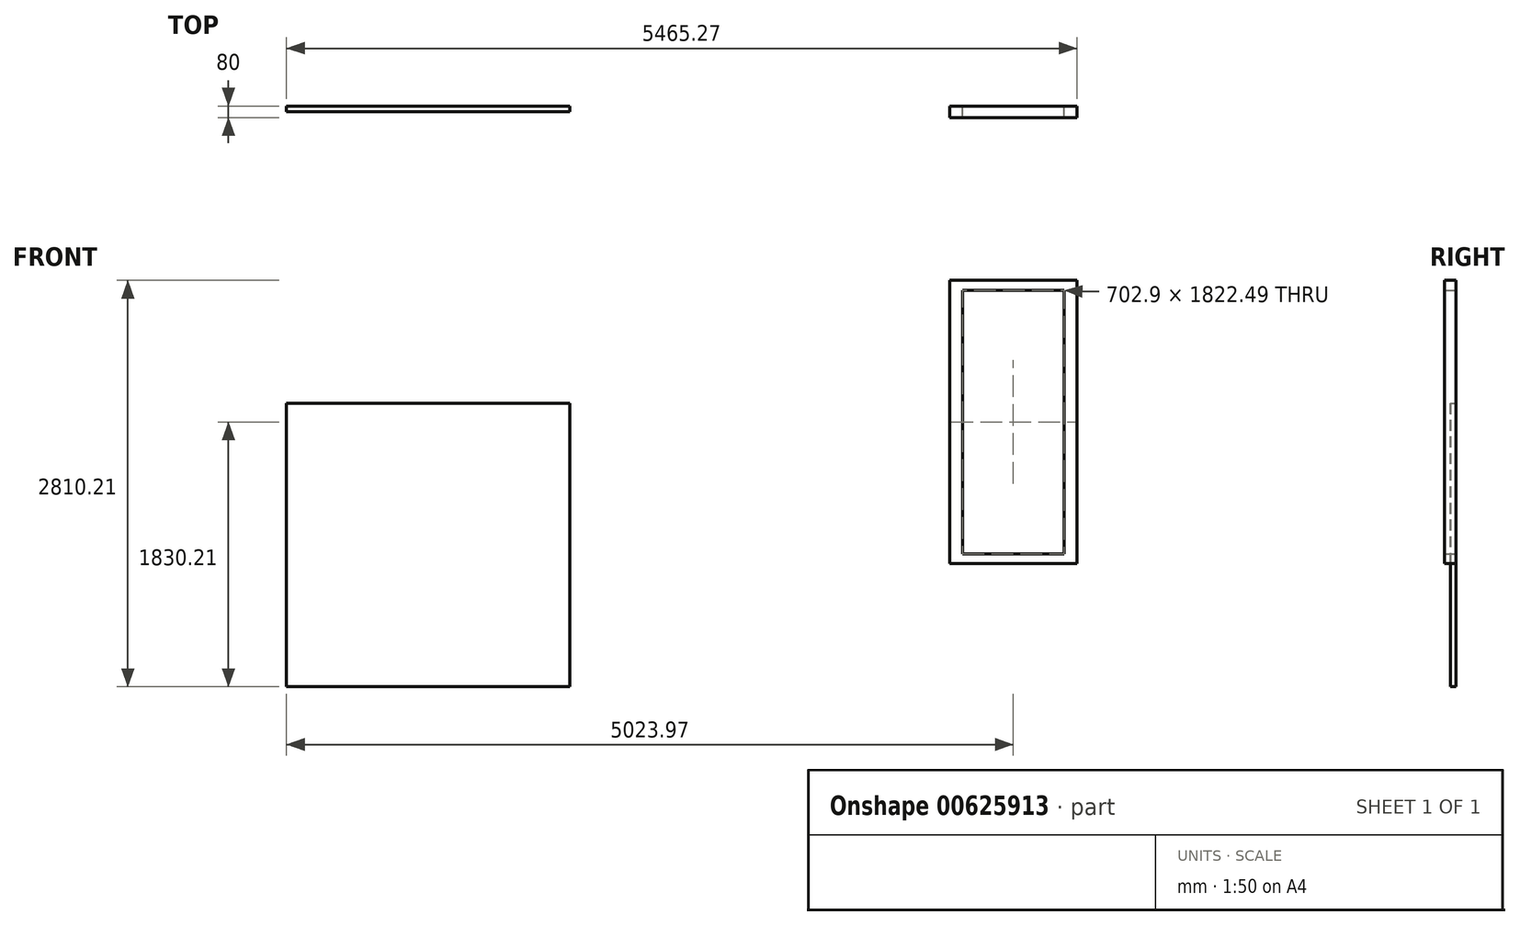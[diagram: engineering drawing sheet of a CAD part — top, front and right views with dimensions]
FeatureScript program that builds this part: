
annotation { "Feature Type Name" : "Feature", "Feature Type Description" : "" }
export const myFeature = defineFeature(function(context is Context, id is Id, definition is map)
    precondition{}
    {
        {
            var Q0;
            Q0=qCreatedBy(makeId("Front.planeOp"),FACE);
            var sketch = newSketch(context, id + "F0", { "sketchPlane" : qUnion([Q0])});
            skLineSegment(sketch, "E0", {"start": v(-2908.04, -1960) * mm, "end": v(-2908.04, 0) * mm});
            skLineSegment(sketch, "E1", {"start": v(-2908.04, 0) * mm, "end": v(-4868.04, 0) * mm});
            skLineSegment(sketch, "E2", {"start": v(-4868.04, 0) * mm, "end": v(-4868.04, -1960) * mm});
            skLineSegment(sketch, "E3", {"start": v(-4868.04, -1960) * mm, "end": v(-2908.04, -1960) * mm});
            skSolve(sketch);
        }
        {
            var Q0;
            Q0=makeQuery(id+"F0.imprint","IMPRINT",FACE,{"disambiguationData":[TD([[makeQuery(id+"F0.imprint","IMPRINT",EDGE,{"derivedFrom":sQuery(id+"F0.wireOp",EDGE,"E0")}),1.0]])]});
            extrude(context, id + "F1", {"entities" : qUnion([Q0]), "depth" : 38 * mm, "offsetDistance" : 25 * mm});
        }
        {
            var Q0;
            Q0=qCreatedBy(makeId("Front.planeOp"),FACE);
            var sketch = newSketch(context, id + "F2", { "sketchPlane" : qUnion([Q0])});
            skLineSegment(sketch, "E4", {"start": v(-285.37, -1109.8) * mm, "end": v(-285.37, 850.2) * mm});
            skLineSegment(sketch, "E5", {"start": v(-285.37, 850.2) * mm, "end": v(-195.52, 850.2) * mm});
            skLineSegment(sketch, "E6", {"start": v(-285.37, -1109.8) * mm, "end": v(-195.52, -1041.04) * mm});
            skLineSegment(sketch, "E7", {"start": v(-285.37, -1109.8) * mm, "end": v(597.23, -1109.8) * mm});
            skLineSegment(sketch, "E8", {"start": v(597.23, -1109.8) * mm, "end": v(597.23, 850.2) * mm});
            skLineSegment(sketch, "E9", {"start": v(597.23, 850.2) * mm, "end": v(-195.52, 850.2) * mm});
            skLineSegment(sketch, "E10", {"start": v(-195.52, -1041.04) * mm, "end": v(507.38, -1041.04) * mm});
            skLineSegment(sketch, "E11", {"start": v(507.38, -1041.04) * mm, "end": v(507.38, 781.45) * mm});
            skLineSegment(sketch, "E12", {"start": v(507.38, 781.45) * mm, "end": v(-195.52, 781.45) * mm});
            skLineSegment(sketch, "E13", {"start": v(507.38, -1041.04) * mm, "end": v(597.23, -1109.8) * mm});
            skLineSegment(sketch, "E14", {"start": v(507.38, 781.45) * mm, "end": v(597.23, 850.2) * mm});
            skLineSegment(sketch, "E15", {"start": v(-195.52, 781.45) * mm, "end": v(-285.37, 850.2) * mm});
            skLineSegment(sketch, "E16", {"start": v(-195.52, -1041.04) * mm, "end": v(-195.52, 781.45) * mm});
            skSolve(sketch);
        }
        {
            var Q0;
            Q0 = qSketchRegion(id + "F2", true);
            extrude(context, id + "F3", {"entities" : qUnion([Q0]), "depth" : 80 * mm, "offsetDistance" : 25 * mm});
        }
    });
